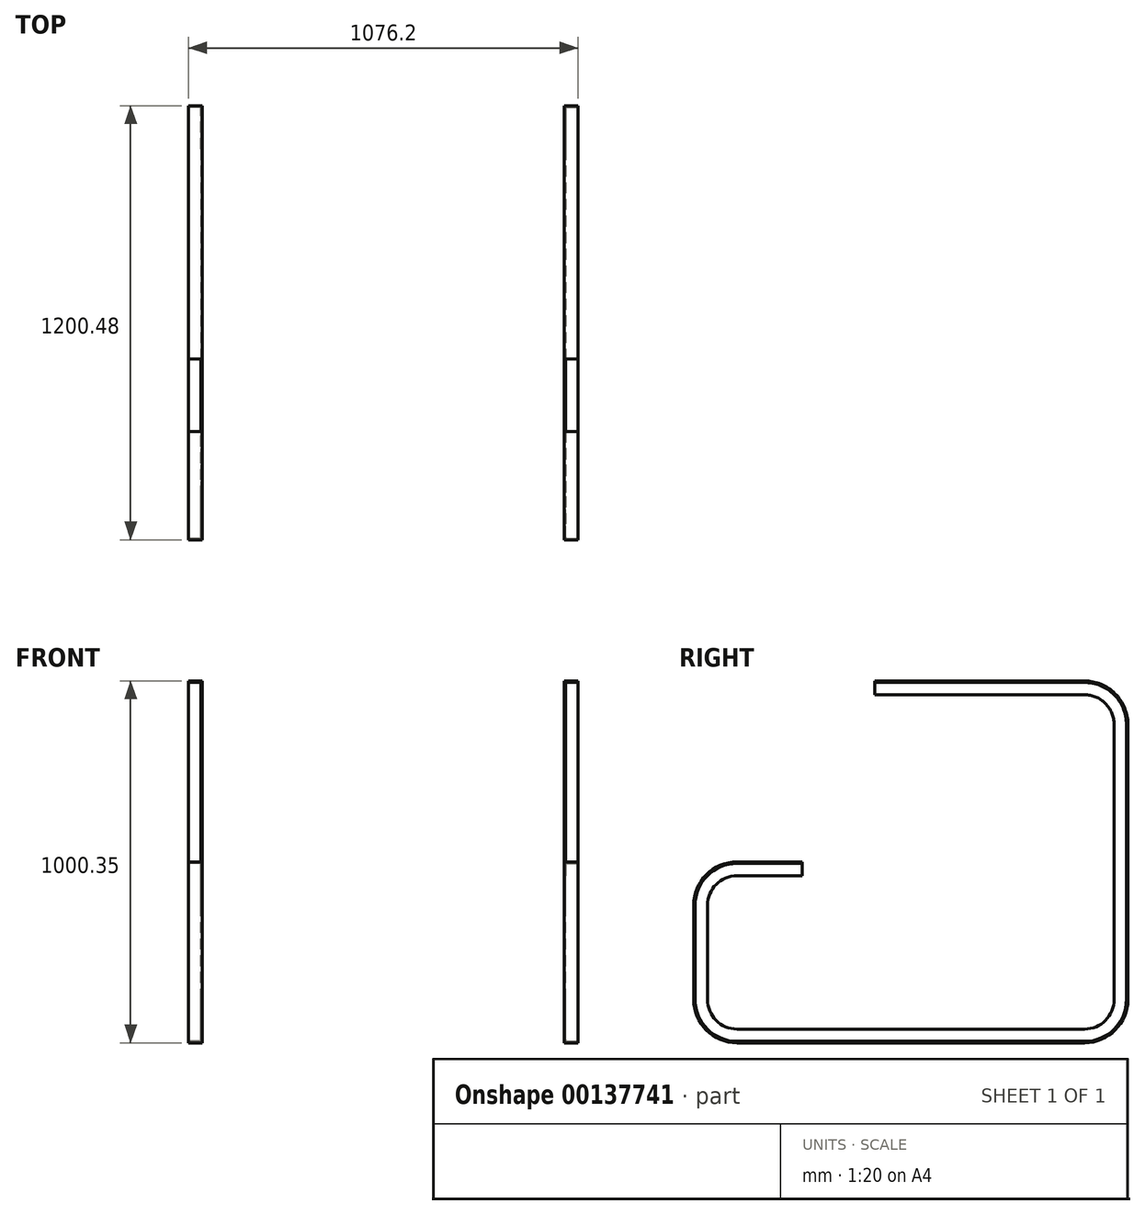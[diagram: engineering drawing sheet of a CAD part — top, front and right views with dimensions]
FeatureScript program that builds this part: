
annotation { "Feature Type Name" : "Feature", "Feature Type Description" : "" }
export const myFeature = defineFeature(function(context is Context, id is Id, definition is map)
    precondition{}
    {
        {
            var Q0;
            Q0=qCreatedBy(makeId("Front.planeOp"),FACE);
            var sketch = newSketch(context, id + "F0", { "sketchPlane" : qUnion([Q0])});
            skLineSegment(sketch, "E0.bottom", {"start": v(0, 0) * mm, "end": v(-38.1, 0) * mm});
            skLineSegment(sketch, "E0.top", {"start": v(0, 38.1) * mm, "end": v(-4, 38.1) * mm});
            skLineSegment(sketch, "E0.left", {"start": v(0, 0) * mm, "end": v(0, 38.1) * mm});
            skLineSegment(sketch, "E0.right", {"start": v(-38.1, 0) * mm, "end": v(-38.1, 4) * mm});
            skLineSegment(sketch, "E1.0", {"start": v(-4, 8) * mm, "end": v(-4, 38.1) * mm});
            skLineSegment(sketch, "E1.1", {"start": v(-8, 4) * mm, "end": v(-38.1, 4) * mm});
            skPoint(sketch, "E2.visualSharp", {"position": v(-4, 4) * mm});
            skArc(sketch, "E2.filletArc", {"start": v(-8, 4) * mm, "mid": v(-5.17, 5.17) * mm, "end": v(-4, 8) * mm});
            skSolve(sketch);
        }
        {
            var Q0;
            Q0=qCreatedBy(makeId("Right.planeOp"),FACE);
            var sketch = newSketch(context, id + "F1", { "sketchPlane" : qUnion([Q0])});
            skLineSegment(sketch, "E3", {"start": v(0, 0) * mm, "end": v(-380.43, 0) * mm});
            skLineSegment(sketch, "E4", {"start": v(-500.43, 120) * mm, "end": v(-500.43, 380) * mm});
            skLineSegment(sketch, "E5", {"start": v(-380.43, 500) * mm, "end": v(-200.43, 500) * mm});
            skPoint(sketch, "E6.visualSharp", {"position": v(-500.43, 500) * mm});
            skArc(sketch, "E6.filletArc", {"start": v(-380.43, 500) * mm, "mid": v(-465.29, 464.85) * mm, "end": v(-500.43, 380) * mm});
            skPoint(sketch, "E7.visualSharp", {"position": v(-500.43, 0) * mm});
            skArc(sketch, "E7.filletArc", {"start": v(-500.43, 120) * mm, "mid": v(-465.29, 35.15) * mm, "end": v(-380.43, 0) * mm});
            skSolve(sketch);
        }
        {
            var Q0;
            Q0=qCreatedBy(makeId("Right.planeOp"),FACE);
            var sketch = newSketch(context, id + "F2", { "sketchPlane" : qUnion([Q0])});
            skLineSegment(sketch, "E8", {"start": v(0, 0) * mm, "end": v(580.05, 0) * mm});
            skLineSegment(sketch, "E9", {"start": v(700.05, 120) * mm, "end": v(700.05, 880.35) * mm});
            skLineSegment(sketch, "E10", {"start": v(579.98, 1000.35) * mm, "end": v(0, 999.99) * mm});
            skPoint(sketch, "E11.visualSharp", {"position": v(700.05, 0) * mm});
            skArc(sketch, "E11.filletArc", {"start": v(580.05, 0) * mm, "mid": v(664.9, 35.15) * mm, "end": v(700.05, 120) * mm});
            skPoint(sketch, "E12.visualSharp", {"position": v(700.05, 1000.42) * mm});
            skArc(sketch, "E12.filletArc", {"start": v(700.05, 880.35) * mm, "mid": v(664.88, 965.23) * mm, "end": v(579.98, 1000.35) * mm});
            skSolve(sketch);
        }
        {
            var Q0;
            Q0 = qSketchRegion(id + "F0", true);
            var Q1;
            Q1 = qConstructionFilter(qBodyType(qCreatedBy(id + "F1" ,EDGE), BodyType.WIRE), ConstructionObject.NO);
            sweep(context, id + "F3", {"profiles" : qUnion([Q0]), "path" : qUnion([Q1])});
        }
        {
            var Q0;
            Q0 = qSketchRegion(id + "F0", true);
            var Q1;
            Q1 = qConstructionFilter(qBodyType(qCreatedBy(id + "F2" ,EDGE), BodyType.WIRE), ConstructionObject.NO);
            sweep(context, id + "F4", {"operationType" : NewBodyOperationType.ADD, "profiles" : qUnion([Q0]), "path" : qUnion([Q1])});
        }
        {
            var Q0;
            Q0=qCreatedBy(makeId("Right.planeOp"),FACE);
            cPlane(context, id + "F5", {"entities" : qUnion([Q0]), "cplaneType" : CPlaneType.OFFSET, "offset" : 500 * mm, "width" : 150 * mm, "height" : 150 * mm});
        }
        {
            var Q0;
            Q0=makeQuery(id+"F3.opSweep","SWEPT_BODY",BODY,{"disambiguationData":[OSD([sQuery(id+"F0.wireOp",EDGE,"E0.bottom"),sQuery(id+"F0.wireOp",EDGE,"E0.top"),sQuery(id+"F0.wireOp",EDGE,"E0.left"),sQuery(id+"F0.wireOp",EDGE,"E0.right"),sQuery(id+"F0.wireOp",EDGE,"E1.0"),sQuery(id+"F0.wireOp",EDGE,"E1.1"),sQuery(id+"F0.wireOp",EDGE,"E2.filletArc"),sQuery(id+"F1.wireOp",EDGE,"E3")])]});
            var Q1;
            Q1=qCreatedBy(id+"F5.planeOp",FACE);
            mirror(context, id + "F6", {"entities" : qUnion([Q0]), "mirrorPlane" : qUnion([Q1])});
        }
    });
